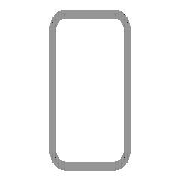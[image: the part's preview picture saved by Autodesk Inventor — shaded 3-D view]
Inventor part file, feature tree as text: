
AUTODESK INVENTOR PART (.ipt)
format: ipt  version: 2025 (Build 290162010, 162A)  size: 134,656 bytes
history: native  units: mm (DEFAULTED — no unit token found)
features: other x4, sketch x1, plane x1
ambient origin geometry x8: Origin, YZ Plane, XZ Plane, XY Plane, X Axis, Y Axis, Z Axis, Center Point
bodies: Solid1 (feature_tree), Body (feature_tree)
feature tree (6):
  parser-record x1  (decoder bookkeeping rows leaked as tree rows — omitted from the tree; the rows remain in map.json)
  other  "Driven Length"
  other  "Start Plane"
  other  "End Plane"
  sketch  "Sketch3"  dims[d3=1295.0mm d4=0.0mm d7=6.0mm d9=40.0mm d11=60.0mm d12=3.0mm d13=40.0mm d14=1335.0mm d15=20.0mm d16=30.0mm d17=90.0deg d18=1295.0mm]
  plane  "Work Plane3"
